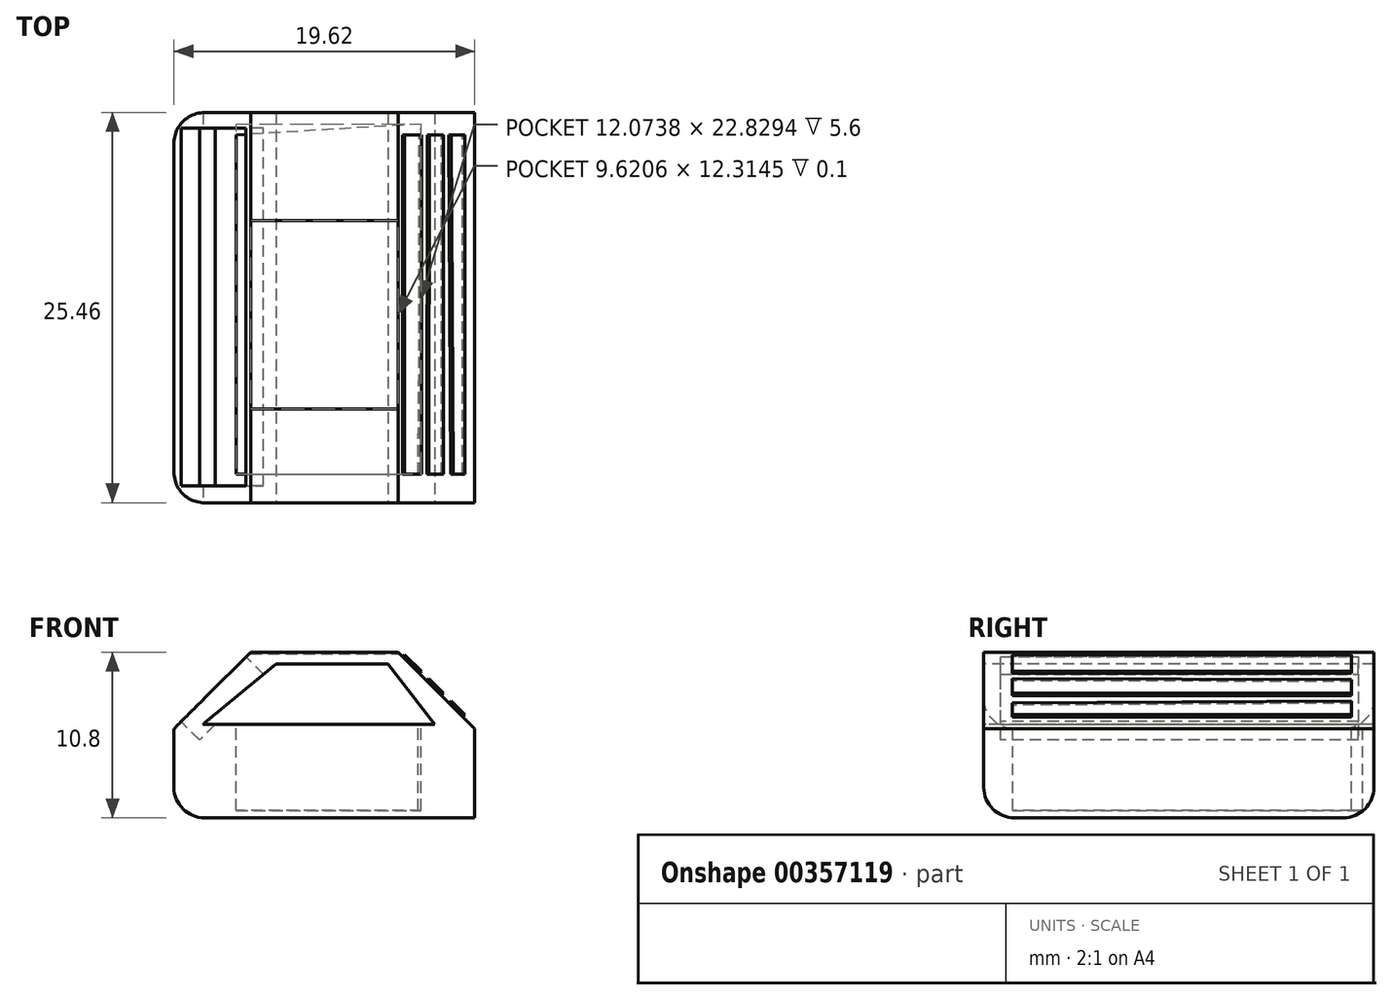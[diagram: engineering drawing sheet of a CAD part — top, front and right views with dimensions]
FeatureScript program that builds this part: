
annotation { "Feature Type Name" : "Feature", "Feature Type Description" : "" }
export const myFeature = defineFeature(function(context is Context, id is Id, definition is map)
    precondition{}
    {
        {
            var Q0;
            Q0=qCreatedBy(makeId("Top.planeOp"),FACE);
            var sketch = newSketch(context, id + "F0", { "sketchPlane" : qUnion([Q0])});
            skLineSegment(sketch, "E0.bottom", {"start": v(-9.81, 12.73) * mm, "end": v(9.81, 12.73) * mm});
            skLineSegment(sketch, "E0.top", {"start": v(-9.81, -12.73) * mm, "end": v(9.81, -12.73) * mm});
            skLineSegment(sketch, "E0.left", {"start": v(-9.81, 12.73) * mm, "end": v(-9.81, -12.73) * mm});
            skLineSegment(sketch, "E0.right", {"start": v(9.81, 12.73) * mm, "end": v(9.81, -12.73) * mm});
            skPoint(sketch, "E0.middle", {"position": v(0, 0) * mm});
            skSolve(sketch);
        }
        {
            var Q0;
            Q0 = qSketchRegion(id + "F0", true);
            extrude(context, id + "F1", {"entities" : qUnion([Q0]), "endBound" : BoundingType.SYMMETRIC, "depth" : 10.8 * mm});
        }
        {
            var Q0;
            Q0=makeQuery(id+"F1.opExtrude","CAP_EDGE",EDGE,{"disambiguationData":[OSD([sQuery(id+"F0.wireOp",EDGE,"E0.left")])],"isStart":false});
            chamfer(context, id + "F2", {"entities" : qUnion([Q0]), "width" : 5 * mm, "tangentPropagation" : true});
        }
        {
            var Q0;
            Q0=makeQuery(id+"F1.opExtrude","CAP_EDGE",EDGE,{"disambiguationData":[OSD([sQuery(id+"F0.wireOp",EDGE,"E0.right")])],"isStart":false});
            chamfer(context, id + "F3", {"entities" : qUnion([Q0]), "width" : 5 * mm, "tangentPropagation" : true});
        }
        {
            var Q0;
            Q0=makeQuery(id+"F3.opChamfer","BLEND_FACE",FACE,{"disambiguationData":[OSD([sQuery(id+"F0.wireOp",EDGE,"E0.right")])]});
            var sketch = newSketch(context, id + "F4", { "sketchPlane" : qUnion([Q0])});
            skLineSegment(sketch, "E1", {"start": v(-10.86, 0) * mm, "end": v(-10.86, -1.54) * mm});
            skLineSegment(sketch, "E2", {"start": v(-10.86, -1.54) * mm, "end": v(11.27, -1.54) * mm});
            skLineSegment(sketch, "E3", {"start": v(11.27, -1.54) * mm, "end": v(11.27, 0) * mm});
            skLineSegment(sketch, "E4", {"start": v(11.27, 0) * mm, "end": v(-10.86, 0) * mm});
            skLineSegment(sketch, "E5", {"start": v(-10.86, -2.23) * mm, "end": v(-10.86, -3.58) * mm});
            skLineSegment(sketch, "E6", {"start": v(-10.86, -3.58) * mm, "end": v(11.27, -3.58) * mm});
            skLineSegment(sketch, "E7", {"start": v(11.27, -3.58) * mm, "end": v(11.27, -2.28) * mm});
            skLineSegment(sketch, "E8", {"start": v(11.27, -2.28) * mm, "end": v(-10.86, -2.23) * mm});
            skLineSegment(sketch, "E9", {"start": v(-10.86, -4.46) * mm, "end": v(-10.86, -5.54) * mm});
            skLineSegment(sketch, "E10", {"start": v(-10.86, -5.54) * mm, "end": v(11.27, -5.54) * mm});
            skLineSegment(sketch, "E11", {"start": v(11.27, -5.54) * mm, "end": v(11.27, -4.28) * mm});
            skLineSegment(sketch, "E12", {"start": v(11.27, -4.28) * mm, "end": v(-10.86, -4.46) * mm});
            skSolve(sketch);
        }
        {
            var Q0;
            Q0 = qSketchRegion(id + "F4", true);
            extrude(context, id + "F5", {"entities" : qUnion([Q0]), "operationType" : NewBodyOperationType.ADD, "depth" : 0.2 * mm});
        }
        {
            var Q0;
            Q0=makeQuery(id+"F1.opExtrude","SWEPT_FACE",FACE,{"disambiguationData":[OSD([sQuery(id+"F0.wireOp",EDGE,"E0.top")])]});
            var sketch = newSketch(context, id + "F6", { "sketchPlane" : qUnion([Q0])});
            skLineSegment(sketch, "E13", {"start": v(-3.16, 4.62) * mm, "end": v(4.14, 4.62) * mm});
            skLineSegment(sketch, "E14", {"start": v(-3.16, 4.62) * mm, "end": v(-7.92, 0.69) * mm});
            skLineSegment(sketch, "E15", {"start": v(-7.92, 0.69) * mm, "end": v(7.2, 0.69) * mm});
            skLineSegment(sketch, "E16", {"start": v(7.2, 0.69) * mm, "end": v(4.14, 4.62) * mm});
            skSolve(sketch);
        }
        {
            var Q0;
            Q0 = qSketchRegion(id + "F6", true);
            extrude(context, id + "F7", {"entities" : qUnion([Q0]), "operationType" : NewBodyOperationType.REMOVE, "oppositeDirection" : true, "depth" : 25.5 * mm});
        }
        {
            var Q0;
            Q0=makeQuery(id+"F2.opChamfer","BLEND_FACE",FACE,{"disambiguationData":[OSD([sQuery(id+"F0.wireOp",EDGE,"E0.left")])]});
            var sketch = newSketch(context, id + "F8", { "sketchPlane" : qUnion([Q0])});
            skLineSegment(sketch, "E17", {"start": v(-11.72, 0) * mm, "end": v(-11.72, -5.98) * mm});
            skLineSegment(sketch, "E18", {"start": v(-11.72, -5.98) * mm, "end": v(11.63, -5.98) * mm});
            skLineSegment(sketch, "E19", {"start": v(11.63, -5.98) * mm, "end": v(11.63, 0) * mm});
            skLineSegment(sketch, "E20", {"start": v(11.63, 0) * mm, "end": v(-11.72, 0) * mm});
            skSolve(sketch);
        }
        {
            var Q0;
            Q0 = qSketchRegion(id + "F8", true);
            extrude(context, id + "F9", {"entities" : qUnion([Q0]), "operationType" : NewBodyOperationType.REMOVE, "oppositeDirection" : true, "depth" : 1.7 * mm});
        }
        {
            var Q0;
            Q0=makeQuery(id+"F1.opExtrude","CAP_EDGE",EDGE,{"disambiguationData":[OSD([sQuery(id+"F0.wireOp",EDGE,"E0.top")])],"isStart":true});
            fillet(context, id + "F10", {"entities" : qUnion([Q0]), "radius" : 2 * mm, "tangentPropagation" : true, "allowEdgeOverflow" : false});
        }
        {
            var Q0;
            Q0=makeQuery(id+"F1.opExtrude","CAP_EDGE",EDGE,{"disambiguationData":[OSD([sQuery(id+"F0.wireOp",EDGE,"E0.left")])],"isStart":true});
            fillet(context, id + "F11", {"entities" : qUnion([Q0]), "radius" : 2 * mm, "tangentPropagation" : true, "allowEdgeOverflow" : false});
        }
        {
            var Q0;
            Q0=makeQuery(id+"F1.opExtrude","CAP_EDGE",EDGE,{"disambiguationData":[OSD([sQuery(id+"F0.wireOp",EDGE,"E0.bottom")])],"isStart":true});
            fillet(context, id + "F12", {"entities" : qUnion([Q0]), "radius" : 2 * mm, "tangentPropagation" : true, "allowEdgeOverflow" : false});
        }
        {
            var Q0;
            Q0=makeQuery(id+"F7.boolean.opBoolean","COPY",FACE,{"derivedFrom":makeQuery(id+"F7.opExtrude","SWEPT_FACE",FACE,{"disambiguationData":[OSD([sQuery(id+"F6.wireOp",EDGE,"E15")])]})});
            var sketch = newSketch(context, id + "F13", { "sketchPlane" : qUnion([Q0])});
            skLineSegment(sketch, "E21", {"start": v(6.32, 11.98) * mm, "end": v(-5.75, 11.27) * mm});
            skLineSegment(sketch, "E22", {"start": v(-5.75, 11.27) * mm, "end": v(-5.75, -10.85) * mm});
            skLineSegment(sketch, "E23", {"start": v(-5.75, -10.85) * mm, "end": v(6.11, -10.85) * mm});
            skLineSegment(sketch, "E24", {"start": v(6.11, -10.85) * mm, "end": v(6.32, 11.98) * mm});
            skSolve(sketch);
        }
        {
            var Q0;
            Q0 = qSketchRegion(id + "F13", true);
            extrude(context, id + "F14", {"entities" : qUnion([Q0]), "operationType" : NewBodyOperationType.REMOVE, "oppositeDirection" : true, "depth" : 5.6 * mm});
        }
        {
            var Q0;
            Q0=makeQuery(id+"F1.opExtrude","CAP_FACE",FACE,{"disambiguationData":[OSD([sQuery(id+"F0.wireOp",EDGE,"E0.bottom"),sQuery(id+"F0.wireOp",EDGE,"E0.top"),sQuery(id+"F0.wireOp",EDGE,"E0.left"),sQuery(id+"F0.wireOp",EDGE,"E0.right")])],"isStart":false});
            var sketch = newSketch(context, id + "F15", { "sketchPlane" : qUnion([Q0])});
            skLineSegment(sketch, "E25", {"start": v(-4.81, 5.7) * mm, "end": v(4.81, 5.7) * mm});
            skLineSegment(sketch, "E26", {"start": v(-4.81, -6.62) * mm, "end": v(4.81, -6.62) * mm});
            skLineSegment(sketch, "E27", {"start": v(-4.81, 5.7) * mm, "end": v(-4.81, -6.62) * mm});
            skLineSegment(sketch, "E28", {"start": v(4.81, 5.7) * mm, "end": v(4.81, -6.62) * mm});
            skSolve(sketch);
        }
        {
            var Q0;
            Q0 = qSketchRegion(id + "F15", true);
            extrude(context, id + "F16", {"entities" : qUnion([Q0]), "operationType" : NewBodyOperationType.REMOVE, "oppositeDirection" : true, "depth" : 0.1 * mm});
        }
    });
